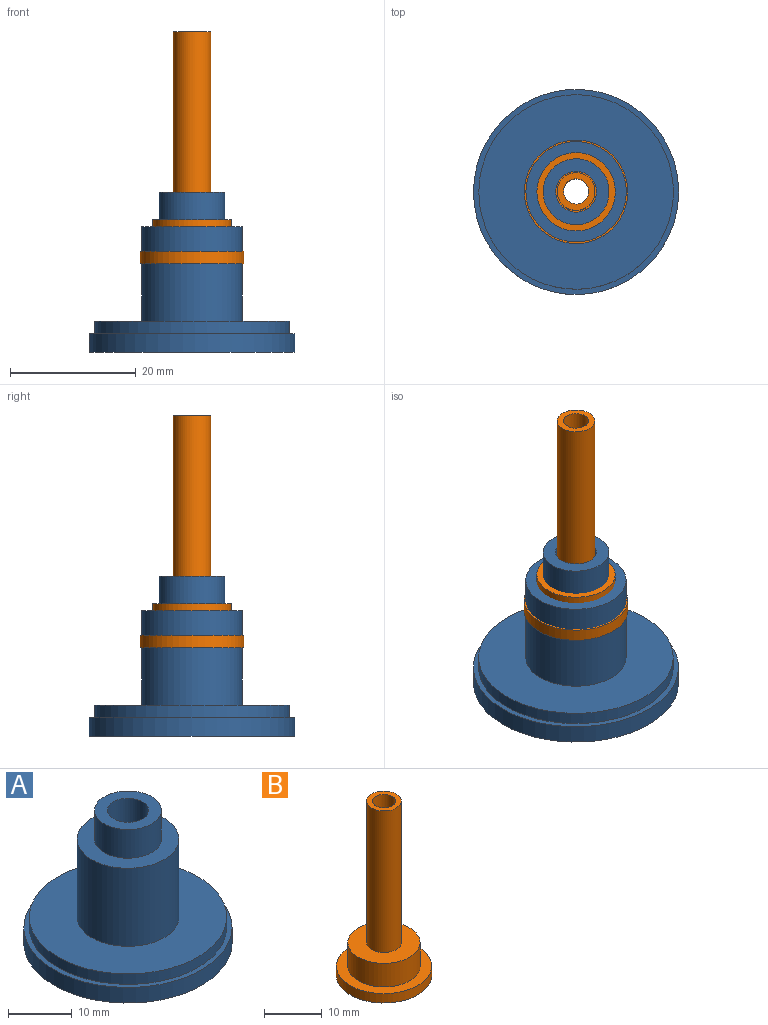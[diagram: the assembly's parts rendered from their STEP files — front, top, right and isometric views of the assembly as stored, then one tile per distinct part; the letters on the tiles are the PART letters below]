
ASSEMBLY  parts=2 mates=1
PART A: 12 faces, bbox 32.7x32.7x25.5 mm
  f0: plane 32.7x32.7mm, normal (0,0,-1), area 726.7mm2, adj f1,f11
  f1: cylinder r=6mm len=18mm, axis (0,0,-1), area 678.6mm2, adj f0,f2
  f2: plane 12x12mm, normal (0,0,-1), area 79.9mm2, adj f1,f3
  f3: cylinder r=3.25mm len=7.5mm, axis (0,0,-1), area 153.2mm2, adj f2,f4
  f4: plane 10.5x10.5mm, normal (0,0,1), area 53.4mm2, adj f3,f5
  f5: cylinder r=5.25mm len=10.5mm, axis (0,0,-1), area 181.4mm2, adj f4,f6
  f6: plane 16x16mm, normal (0,0,1), area 114.5mm2, adj f5,f7
  f7: cylinder r=8mm len=16mm, axis (0,0,-1), area 754mm2, adj f6,f8
  f8: plane 31x31mm, normal (0,0,1), area 553.7mm2, adj f7,f9
  f9: cylinder r=15.5mm len=31mm, axis (0,0,-1), area 194.8mm2, adj f8,f10
  f10: plane 32.7x32.7mm, normal (0,0,1), area 85.1mm2, adj f9,f11
  f11: cylinder r=16.35mm len=32.7mm, axis (0,0,-1), area 308.2mm2, adj f0,f10
PART B: 10 faces, bbox 16.5x16.5x37 mm
  f0: plane 8.5x8.5mm, normal (0,0,-1), area 44.2mm2, adj f1,f9
  f1: cylinder r=4.25mm len=8.5mm, axis (0,0,-1), area 133.5mm2, adj f0,f2
  f2: plane 16.5x16.5mm, normal (0,0,-1), area 157.1mm2, adj f1,f3
  f3: cylinder r=8.25mm len=16.5mm, axis (0,0,-1), area 103.7mm2, adj f2,f4
  f4: plane 16.5x16.5mm, normal (0,0,1), area 91.1mm2, adj f3,f5
  f5: cylinder r=6.25mm len=12.5mm, axis (0,0,-1), area 196.3mm2, adj f4,f6
  f6: plane 12.5x12.5mm, normal (0,0,1), area 94.4mm2, adj f5,f7
  f7: cylinder r=3mm len=30mm, axis (0,0,-1), area 565.5mm2, adj f6,f8
  f8: plane 6x6mm, normal (0,0,1), area 15.7mm2, adj f7,f9
  f9: cylinder r=2mm len=32mm, axis (0,0,-1), area 402.1mm2, adj f0,f8
PLACE A t=(-23.75,-7.84,4.59)mm fixed
PLACE B rot(axis=(0,0,1),98.8deg) t=(-23.75,-7.84,18.71)mm
MATE cylindrical B.f1 <-> A.f1  axis (0,0,-1) through (-23.75,-7.84,23.21)mm
